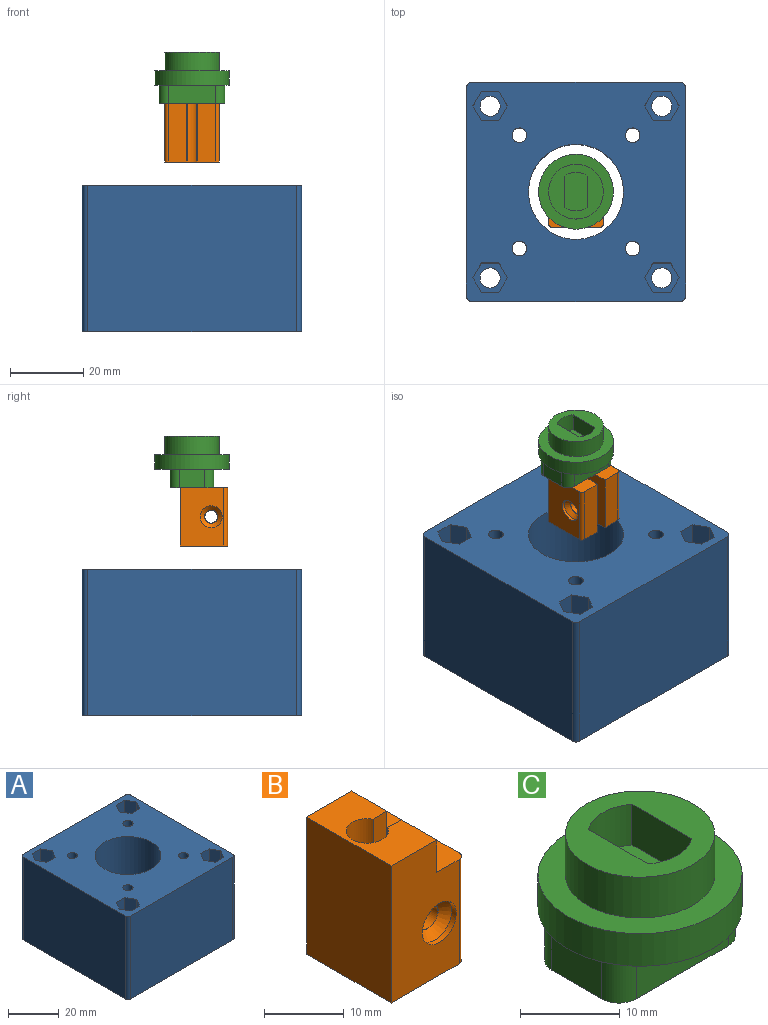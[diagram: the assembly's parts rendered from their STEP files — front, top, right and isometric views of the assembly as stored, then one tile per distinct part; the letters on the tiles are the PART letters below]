
ASSEMBLY  parts=3 mates=2
PART A: 59 faces, bbox 60x60x40 mm
  f0: plane 60x60mm, normal (0,0,-1), area 2771mm2, adj f6,f7,f8,f9,f10,f11,f12,f13
  f1: cylinder r=2mm len=22mm, axis (0,0,1), area 276.5mm2, adj f5,f53
  f2: cylinder r=2mm len=22mm, axis (0,0,1), area 276.5mm2, adj f5,f52
  f3: cylinder r=2mm len=22mm, axis (0,0,1), area 276.5mm2, adj f5,f50
  f4: cylinder r=2mm len=22mm, axis (0,0,1), area 276.5mm2, adj f5,f48
  f5: plane 60x60mm, normal (0,0,1), area 2783.9mm2, adj f1,f2,f3,f4,f10,f11,f12,f13
  f6: cylinder r=2.75mm len=5.5mm, axis (0,0,1), area 34.6mm2, adj f0,f40
  f7: cylinder r=2.75mm len=5.5mm, axis (0,0,1), area 34.6mm2, adj f0,f39
  f8: cylinder r=2.75mm len=5.5mm, axis (0,0,1), area 34.6mm2, adj f0,f26
  f9: cylinder r=2.75mm len=5.5mm, axis (0,0,1), area 34.6mm2, adj f0,f25
  f10: plane 57x40mm, normal (0,1,0), area 2280mm2, adj f0,f5,f15,f18
  f11: plane 57x40mm, normal (-1,0,0), area 2280mm2, adj f0,f5,f15,f16
  f12: plane 57x40mm, normal (0,-1,0), area 2280mm2, adj f0,f5,f16,f17
  f13: plane 57x40mm, normal (1,0,0), area 2280mm2, adj f0,f5,f17,f18
  f14: cylinder r=13mm len=40mm, axis (0,0,1), area 3267.3mm2, adj f0,f5
  f15: cylinder r=1.5mm len=40mm, axis (0,0,1), area 94.2mm2, adj f0,f5,f10,f11
  f16: cylinder r=1.5mm len=40mm, axis (0,0,-1), area 94.2mm2, adj f0,f5,f11,f12
  f17: cylinder r=1.5mm len=40mm, axis (0,0,1), area 94.2mm2, adj f0,f5,f12,f13
  f18: cylinder r=1.5mm len=40mm, axis (0,0,-1), area 94.2mm2, adj f0,f5,f10,f13
  f19: plane 38x4.1mm, normal (-0.87,-0.5,0), area 179.9mm2, adj f5,f20,f24,f25
  f20: plane 38x4.73mm, normal (0,-1,0), area 179.9mm2, adj f5,f19,f21,f25
  f21: plane 38x4.1mm, normal (0.87,-0.5,0), area 179.9mm2, adj f5,f20,f22,f25
  f22: plane 38x4.1mm, normal (0.87,0.5,0), area 179.9mm2, adj f5,f21,f23,f25
  f23: plane 38x4.73mm, normal (0,1,0), area 179.9mm2, adj f5,f22,f24,f25
  f24: plane 38x4.1mm, normal (-0.87,0.5,0), area 179.9mm2, adj f5,f19,f23,f25
  f25: plane 9.47x8.2mm, normal (0,0,1), area 34.5mm2, adj f9,f19,f20,f21,f22,f23,f24
  f26: plane 9.47x8.2mm, normal (0,0,1), area 34.5mm2, adj f8,f27,f28,f29,f30,f31,f32
  f27: plane 38x4.73mm, normal (0,-1,0), area 179.9mm2, adj f5,f26,f28,f32
  f28: plane 38x4.1mm, normal (0.87,-0.5,0), area 179.9mm2, adj f5,f26,f27,f29
  f29: plane 38x4.1mm, normal (0.87,0.5,0), area 179.9mm2, adj f5,f26,f28,f30
  f30: plane 38x4.73mm, normal (0,1,0), area 179.9mm2, adj f5,f26,f29,f31
  f31: plane 38x4.1mm, normal (-0.87,0.5,0), area 179.9mm2, adj f5,f26,f30,f32
  f32: plane 38x4.1mm, normal (-0.87,-0.5,0), area 179.9mm2, adj f5,f26,f27,f31
  f33: plane 38x4.73mm, normal (0,1,0), area 179.9mm2, adj f5,f34,f38,f39
  f34: plane 38x4.1mm, normal (-0.87,0.5,0), area 179.9mm2, adj f5,f33,f35,f39
  f35: plane 38x4.1mm, normal (-0.87,-0.5,0), area 179.9mm2, adj f5,f34,f36,f39
  f36: plane 38x4.73mm, normal (0,-1,0), area 179.9mm2, adj f5,f35,f37,f39
  f37: plane 38x4.1mm, normal (0.87,-0.5,0), area 179.9mm2, adj f5,f36,f38,f39
  f38: plane 38x4.1mm, normal (0.87,0.5,0), area 179.9mm2, adj f5,f33,f37,f39
  f39: plane 9.47x8.2mm, normal (0,0,1), area 34.5mm2, adj f7,f33,f34,f35,f36,f37,f38
  f40: plane 9.47x8.2mm, normal (0,0,1), area 34.5mm2, adj f6,f41,f42,f43,f44,f45,f46
  f41: plane 38x4.73mm, normal (0,1,0), area 179.9mm2, adj f5,f40,f42,f46
  f42: plane 38x4.1mm, normal (-0.87,0.5,0), area 179.9mm2, adj f5,f40,f41,f43
  f43: plane 38x4.1mm, normal (-0.87,-0.5,0), area 179.9mm2, adj f5,f40,f42,f44
  f44: plane 38x4.73mm, normal (0,-1,0), area 179.9mm2, adj f5,f40,f43,f45
  f45: plane 38x4.1mm, normal (0.87,-0.5,0), area 179.9mm2, adj f5,f40,f44,f46
  f46: plane 38x4.1mm, normal (0.87,0.5,0), area 179.9mm2, adj f5,f40,f41,f45
  f47: cylinder r=4mm len=16.1mm, axis (0,0,-1), area 404.6mm2, adj f0,f56
  f48: plane 4.2x4.2mm, normal (0,0,-1), area 1.3mm2, adj f4,f56
  f49: cylinder r=4mm len=16.1mm, axis (0,0,-1), area 404.6mm2, adj f0,f55
  f50: plane 4.2x4.2mm, normal (0,0,-1), area 1.3mm2, adj f3,f55
  f51: cylinder r=4mm len=16.1mm, axis (0,0,-1), area 404.6mm2, adj f0,f57
  f52: plane 4.2x4.2mm, normal (0,0,-1), area 1.3mm2, adj f2,f57
  f53: plane 4.2x4.2mm, normal (0,0,-1), area 1.3mm2, adj f1,f58
  f54: cylinder r=4mm len=16.1mm, axis (0,0,-1), area 404.6mm2, adj f0,f58
  f55: torus R=2.1mm, axis (0,0,-1), area 62.1mm2, adj f49,f50
  f56: torus R=2.1mm, axis (0,0,-1), area 62.1mm2, adj f47,f48
  f57: torus R=2.1mm, axis (0,0,-1), area 62.1mm2, adj f51,f52
  f58: torus R=2.1mm, axis (0,0,-1), area 62.1mm2, adj f53,f54
PART B: 28 faces, bbox 13x15x21 mm
  f0: cylinder r=1.75mm len=4.19mm, axis (0,-1,0), area 45.5mm2, adj f11,f24
  f1: plane 21x12mm, normal (0,1,0), area 200.8mm2, adj f5,f6,f8,f14,f15,f16,f17,f18
  f2: cylinder r=1.75mm len=4.19mm, axis (0,-1,0), area 45.5mm2, adj f10,f22
  f3: plane 16x5mm, normal (1,0,0), area 80mm2, adj f5,f11,f12,f26
  f4: plane 16x5mm, normal (1,0,0), area 80mm2, adj f5,f10,f15,f27
  f5: plane 15x13mm, normal (0,0,-1), area 152.5mm2, adj f1,f3,f4,f6,f7,f9,f10,f11
  f6: plane 21x15mm, normal (-1,0,0), area 315mm2, adj f1,f5,f7,f8
  f7: plane 21x12mm, normal (0,-1,0), area 203.7mm2, adj f5,f6,f8,f12,f13,f23,f26
  f8: plane 15x8mm, normal (0,0,1), area 92.1mm2, adj f1,f6,f7,f9,f10,f11,f13,f14
  f9: cylinder r=2.65mm len=21mm, axis (0,0,1), area 293.9mm2, adj f5,f8,f10,f11
  f10: plane 21x7.43mm, normal (0.03,-1,0), area 121.4mm2, adj f2,f4,f5,f8,f9,f14,f15
  f11: plane 21x7.43mm, normal (0.03,1,0), area 121.4mm2, adj f0,f3,f5,f8,f9,f12,f13
  f12: plane 6.15x5mm, normal (0,0,1), area 30.2mm2, adj f3,f7,f11,f13,f26
  f13: plane 6.15x5mm, normal (1,0,0), area 30.8mm2, adj f7,f8,f11,f12
  f14: plane 6.15x5mm, normal (1,0,0), area 30.8mm2, adj f1,f8,f10,f15
  f15: plane 6.15x5mm, normal (0,0,1), area 30.2mm2, adj f1,f4,f10,f14,f27
  f16: plane 3.46x2mm, normal (0,0,-1), area 6.9mm2, adj f1,f17,f21,f22
  f17: plane 3x2mm, normal (-0.87,0,-0.5), area 6.9mm2, adj f1,f16,f18,f22
  f18: plane 3x2mm, normal (-0.87,0,0.5), area 6.9mm2, adj f1,f17,f19,f22
  f19: plane 3.46x2mm, normal (0,0,1), area 6.9mm2, adj f1,f18,f20,f22
  f20: plane 3x2mm, normal (0.87,0,0.5), area 6.9mm2, adj f1,f19,f21,f22
  f21: plane 3x2mm, normal (0.87,0,-0.5), area 6.9mm2, adj f1,f16,f20,f22
  f22: plane 6.93x6mm, normal (0,1,0), area 21.6mm2, adj f2,f16,f17,f18,f19,f20,f21
  f23: cylinder r=3mm len=6mm, axis (0,-1,0), area 15.1mm2, adj f7,f25
  f24: plane 3.6x3.6mm, normal (0,-1,0), area 0.6mm2, adj f0,f25
  f25: cone r=1.8mm half-angle=45deg, axis (0,-1,0), area 25.6mm2, adj f23,f24
  f26: cylinder r=1mm len=16mm, axis (0,0,1), area 25.1mm2, adj f3,f5,f7,f12
  f27: cylinder r=1mm len=16mm, axis (0,0,-1), area 25.1mm2, adj f1,f4,f5,f15
PART C: 24 faces, bbox 20.5x20.5x14 mm
  f0: plane 15x15mm, normal (0,0,1), area 115.5mm2, adj f14,f15,f16,f17,f18
  f1: plane 20.5x20.5mm, normal (0,0,-1), area 119.4mm2, adj f2,f4,f5,f6,f7,f20,f21,f22
  f2: cylinder r=10.25mm len=20.5mm, axis (0,0,-1), area 257.6mm2, adj f1,f3
  f3: plane 20.5x20.5mm, normal (0,0,1), area 153.3mm2, adj f2,f14
  f4: plane 13x5mm, normal (0,-1,0), area 65mm2, adj f1,f8,f20,f21
  f5: plane 7x5mm, normal (-1,0,0), area 35mm2, adj f1,f8,f20,f22
  f6: plane 13x5mm, normal (0,1,0), area 65mm2, adj f1,f8,f22,f23
  f7: plane 7x5mm, normal (1,0,0), area 35mm2, adj f1,f8,f21,f23
  f8: plane 18x12mm, normal (0,0,-1), area 81.3mm2, adj f4,f5,f6,f7,f9,f10,f11,f12
  f9: plane 15.4x5mm, normal (0,1,0), area 77mm2, adj f8,f10,f12,f13
  f10: plane 8.4x5mm, normal (1,0,0), area 42mm2, adj f8,f9,f11,f13
  f11: plane 15.4x5mm, normal (0,-1,0), area 77mm2, adj f8,f10,f12,f13
  f12: plane 8.4x5mm, normal (-1,0,0), area 42mm2, adj f8,f9,f11,f13
  f13: plane 15.4x8.4mm, normal (0,0,-1), area 129.4mm2, adj f9,f10,f11,f12
  f14: cylinder r=7.5mm len=15mm, axis (0,0,-1), area 235.6mm2, adj f0,f3
  f15: plane 8.5x5mm, normal (-1,0,0), area 42.5mm2, adj f0,f16,f18,f19
  f16: cylinder r=5.26mm len=6.2mm, axis (0,0,1), area 33.2mm2, adj f0,f15,f17,f19
  f17: plane 8.5x5mm, normal (1,0,0), area 42.5mm2, adj f0,f16,f18,f19
  f18: cylinder r=5.26mm len=6.2mm, axis (0,0,1), area 33.2mm2, adj f0,f15,f17,f19
  f19: plane 10.52x6.2mm, normal (0,0,1), area 61.2mm2, adj f15,f16,f17,f18
  f20: cylinder r=2.5mm len=5mm, axis (0,0,-1), area 19.6mm2, adj f1,f4,f5,f8
  f21: cylinder r=2.5mm len=5mm, axis (0,0,1), area 19.6mm2, adj f1,f4,f7,f8
  f22: cylinder r=2.5mm len=5mm, axis (0,0,1), area 19.6mm2, adj f1,f5,f6,f8
  f23: cylinder r=2.5mm len=5mm, axis (0,0,-1), area 19.6mm2, adj f1,f6,f7,f8
PLACE A t=(-11.42,1.91,10.75)mm fixed
PLACE B rot(axis=(0,0,-1),90deg) t=(-11.42,-1.34,57.16)mm
PLACE C t=(-11.42,1.91,78.16)mm
MATE slider A.f14 <-> B.f9  axis (0,0,1) through (-11.42,1.91,10.75)mm
MATE fastened B.f9 <-> C.f14  axis (0,0,1) through (-11.42,1.91,78.16)mm
